# Revit family: 304_Cim3739G-_
name_source: partatom
category: Pipe Accessories
revit_build: Autodesk Revit 2017 (Build: 20160225_1515(x64)
units: mm (PartAtom-declared; Revit-internal decimal feet)

## family parameters
Always vertical = Yes
Cut with Voids When Loaded = No
Part Type = Valve - Breaks Into
Round Connector Dimension = Use Diameter
Shared = No
Work Plane-Based = No

## types (10) — shared parameters
CAT0 = Yes
Description = BALANCING VALVE - VARIABLE ORIFICE - PN 16 - CAST IRON - GROOVED END
HH6 = 35 mm  [stored 0.114829 ft]
HH9 = 20 mm  [stored 0.0656168 ft]
L2D_Min = 3048 mm
Manufacturer = Cimberio
QmdConnectorList = 301;D;302;D
URL = www.cimberio.it
magiPartTypeId = 304
magiProductFamilyId = Cim3739G-*
zero-valued in all types: MC_Default_elevation

## per-type parameters (varying)
- Cim3739G-40: C=7 mm  [stored 0.0229659 ft]; CAT1=Yes; CAT2=No; C__ve=-7 mm  [stored -0.0229659 ft]; D=40 mm; D1=100 mm; DD1=45 mm  [stored 0.147638 ft]; DD3=50 mm  [stored 0.164042 ft]; DD4=36 mm  [stored 0.11811 ft]; DD5=14 mm  [stored 0.0459318 ft]; DD6=140 mm; E=50 mm  [stored 0.164042 ft]; F=45 mm  [stored 0.147638 ft]; G=48 mm  [stored 0.15748 ft]; H=178 mm; H1=100 mm; HH1=156 mm; HH4=83 mm; HH5=50 mm  [stored 0.164042 ft]; HH7=93 mm; HH7__ve=-93 mm  [stored -0.305118 ft]; HH8=167 mm; L2D=200 mm; LL1=100 mm; LL2=168 mm; LL3=47 mm; LL6=60 mm  [stored 0.19685 ft]; S=16 mm  [stored 0.0524934 ft]; S__ve=-16 mm  [stored -0.0524934 ft]; W2D=40 mm  [stored 0.131234 ft]
- Cim3739G-300: C=12 mm  [stored 0.0393701 ft]; CAT1=No; CAT2=Yes; C__ve=-12 mm  [stored -0.0393701 ft]; D=300 mm; D1=425 mm; DD1=306 mm; DD3=350 mm; DD4=254 mm; DD5=64 mm; DD6=644 mm; E=340 mm; F=318 mm; G=324 mm; H=716 mm; H1=460 mm; HH1=694 mm; HH4=393 mm; HH5=213 mm; HH7=434 mm; HH7__ve=-434 mm; HH8=553 mm; L2D=850 mm; LL1=425 mm; LL2=812 mm; LL3=274 mm; LL6=255 mm; S=19 mm  [stored 0.062336 ft]; S__ve=-19 mm  [stored -0.062336 ft]; W2D=300 mm
- Cim3739G-250: C=12 mm  [stored 0.0393701 ft]; CAT1=No; CAT2=Yes; C__ve=-12 mm  [stored -0.0393701 ft]; D=250 mm; D1=365 mm; DD1=258 mm; DD3=295 mm; DD4=214 mm; DD5=57 mm  [stored 0.187008 ft]; DD6=567 mm; E=287 mm; F=268 mm; G=273 mm; H=698 mm; H1=405 mm; HH1=676 mm; HH4=383 mm; HH5=183 mm; HH7=441 mm; HH7__ve=-441 mm; HH8=522 mm; L2D=730 mm; LL1=365 mm; LL2=692 mm; LL3=288 mm; LL6=219 mm; S=19 mm  [stored 0.062336 ft]; S__ve=-19 mm  [stored -0.062336 ft]; W2D=250 mm
- Cim3739G-200: C=12 mm  [stored 0.0393701 ft]; CAT1=No; CAT2=Yes; C__ve=-12 mm  [stored -0.0393701 ft]; D=200 mm; D1=300 mm; DD1=207 mm; DD3=235 mm; DD4=171 mm; DD5=48 mm  [stored 0.15748 ft]; DD6=476 mm; E=230 mm; F=214 mm; G=219 mm; H=655 mm; H1=340 mm; HH1=633 mm; HH4=358 mm; HH5=150 mm; HH7=430 mm; HH7__ve=-430 mm  [stored -1.41076 ft]; HH8=474 mm; L2D=600 mm; LL1=300 mm; LL2=562 mm; LL3=271 mm; LL6=180 mm; S=19 mm  [stored 0.062336 ft]; S__ve=-19 mm  [stored -0.062336 ft]; W2D=200 mm
- Cim3739G-150: C=9 mm  [stored 0.0295276 ft]; CAT1=Yes; CAT2=No; C__ve=-9 mm  [stored -0.0295276 ft]; D=150 mm; D1=240 mm; DD1=156 mm; DD3=177 mm; DD4=129 mm; DD5=14 mm  [stored 0.0459318 ft]; DD6=140 mm; E=173 mm; F=161 mm; G=165 mm; H=403 mm; H1=100 mm; HH1=381 mm; HH4=213 mm; HH5=120 mm; HH7=388 mm; HH7__ve=-388 mm  [stored -1.27297 ft]; HH8=176 mm; L2D=480 mm; LL1=240 mm; LL2=448 mm; LL3=102 mm; LL6=144 mm; S=16 mm  [stored 0.0524934 ft]; S__ve=-16 mm  [stored -0.0524934 ft]; W2D=150 mm
- Cim3739G-125: C=9 mm  [stored 0.0295276 ft]; CAT1=Yes; CAT2=No; C__ve=-9 mm  [stored -0.0295276 ft]; D=125 mm; D1=200 mm; DD1=132 mm; DD3=149 mm; DD4=108 mm; DD5=14 mm  [stored 0.0459318 ft]; DD6=140 mm; E=147 mm; F=135 mm; G=140 mm; H=388 mm; H1=100 mm; HH1=366 mm; HH4=204 mm; HH5=100 mm; HH7=353 mm; HH7__ve=-353 mm  [stored -1.15814 ft]; HH8=191 mm; L2D=400 mm; LL1=200 mm; LL2=368 mm; LL3=121 mm; LL6=120 mm; S=16 mm  [stored 0.0524934 ft]; S__ve=-16 mm  [stored -0.0524934 ft]; W2D=125 mm
- Cim3739G-100: C=9 mm  [stored 0.0295276 ft]; CAT1=Yes; CAT2=No; C__ve=-9 mm  [stored -0.0295276 ft]; D=100 mm; D1=175 mm; DD1=108 mm; DD3=121 mm; DD4=88 mm; DD5=14 mm  [stored 0.0459318 ft]; DD6=140 mm; E=120 mm; F=110 mm; G=114 mm; H=334 mm; H1=100 mm; HH1=312 mm; HH4=173 mm; HH5=88 mm; HH7=287 mm; HH7__ve=-287 mm; HH8=184 mm; L2D=350 mm; LL1=175 mm; LL2=318 mm; LL3=101 mm; LL6=105 mm; S=16 mm  [stored 0.0524934 ft]; S__ve=-16 mm  [stored -0.0524934 ft]; W2D=100 mm
- Cim3739G-80: C=9 mm  [stored 0.0295276 ft]; CAT1=Yes; CAT2=No; C__ve=-9 mm  [stored -0.0295276 ft]; D=80 mm; D1=155 mm; DD1=84 mm; DD3=94 mm; DD4=68 mm; DD5=14 mm  [stored 0.0459318 ft]; DD6=140 mm; E=93 mm; F=85 mm; G=89 mm; H=225 mm; H1=100 mm; HH1=203 mm; HH4=110 mm; HH5=78 mm; HH7=168 mm; HH7__ve=-168 mm; HH8=156 mm; L2D=310 mm; LL1=155 mm; LL2=278 mm; LL3=44 mm; LL6=93 mm; S=16 mm  [stored 0.0524934 ft]; S__ve=-16 mm  [stored -0.0524934 ft]; W2D=80 mm
- Cim3739G-65: C=9 mm  [stored 0.0295276 ft]; CAT1=Yes; CAT2=No; C__ve=-9 mm  [stored -0.0295276 ft]; D=65 mm; D1=145 mm; DD1=69 mm; DD3=76 mm; DD4=55 mm; DD5=14 mm  [stored 0.0459318 ft]; DD6=140 mm; E=77 mm; F=69 mm; G=73 mm; H=214 mm; H1=100 mm; HH1=192 mm; HH4=104 mm; HH5=73 mm; HH7=152 mm; HH7__ve=-152 mm; HH8=157 mm; L2D=290 mm; LL1=145 mm; LL2=258 mm; LL3=43 mm; LL6=87 mm; S=16 mm  [stored 0.0524934 ft]; S__ve=-16 mm  [stored -0.0524934 ft]; W2D=65 mm  [stored 0.213255 ft]
- Cim3739G-50: C=9 mm  [stored 0.0295276 ft]; CAT1=Yes; CAT2=No; C__ve=-9 mm  [stored -0.0295276 ft]; D=50 mm; D1=115 mm; DD1=57 mm  [stored 0.187008 ft]; DD3=63 mm; DD4=46 mm; DD5=14 mm  [stored 0.0459318 ft]; DD6=140 mm; E=63 mm; F=57 mm  [stored 0.187008 ft]; G=60 mm  [stored 0.19685 ft]; H=190 mm; H1=100 mm; HH1=168 mm; HH4=90 mm; HH5=58 mm; HH7=113 mm; HH7__ve=-113 mm; HH8=164 mm; L2D=230 mm; LL1=115 mm; LL2=198 mm; LL3=48 mm  [stored 0.15748 ft]; LL6=69 mm; S=16 mm  [stored 0.0524934 ft]; S__ve=-16 mm  [stored -0.0524934 ft]; W2D=50 mm  [stored 0.164042 ft]

note: column(s) folded — value = type name in every type: magiProductCode, magiProductId

note: [stored X ft] marks values corroborated as IEEE doubles in the binary element streams (Revit-internal decimal feet)

## geometry (parser evidence)
native form markers: Sweep x2
no freeform markers — native parametric forms only
